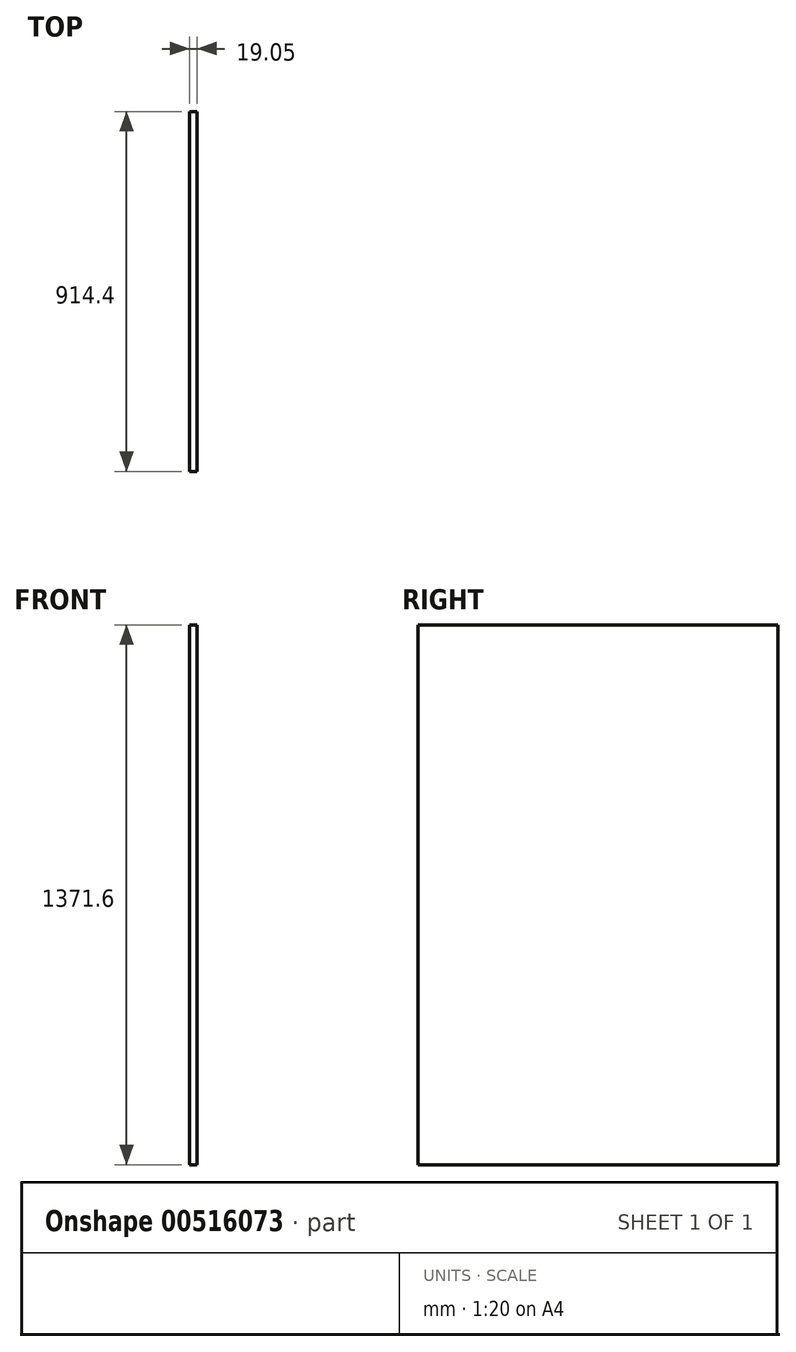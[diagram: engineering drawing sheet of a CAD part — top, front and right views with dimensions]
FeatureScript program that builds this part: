
annotation { "Feature Type Name" : "Feature", "Feature Type Description" : "" }
export const myFeature = defineFeature(function(context is Context, id is Id, definition is map)
    precondition{}
    {
        {
            var Q0;
            Q0=qCreatedBy(makeId("Right.planeOp"),FACE);
            var sketch = newSketch(context, id + "F0", { "sketchPlane" : qUnion([Q0])});
            skLineSegment(sketch, "E0.bottom", {"start": v(457.2, -685.8) * mm, "end": v(-457.2, -685.8) * mm});
            skLineSegment(sketch, "E0.top", {"start": v(457.2, 685.8) * mm, "end": v(-457.2, 685.8) * mm});
            skLineSegment(sketch, "E0.left", {"start": v(457.2, -685.8) * mm, "end": v(457.2, 685.8) * mm});
            skLineSegment(sketch, "E0.right", {"start": v(-457.2, -685.8) * mm, "end": v(-457.2, 685.8) * mm});
            skPoint(sketch, "E0.middle", {"position": v(0, 0) * mm});
            skSolve(sketch);
        }
        {
            var Q0;
            Q0=makeQuery(id+"F0.imprint","IMPRINT",FACE,{"disambiguationData":[TD([[makeQuery(id+"F0.imprint","IMPRINT",EDGE,{"derivedFrom":sQuery(id+"F0.wireOp",EDGE,"E0.bottom")}),-1.0]])]});
            extrude(context, id + "F1", {"entities" : qUnion([Q0]), "depth" : 19.05 * mm, "offsetDistance" : 25.4 * mm});
        }
    });
